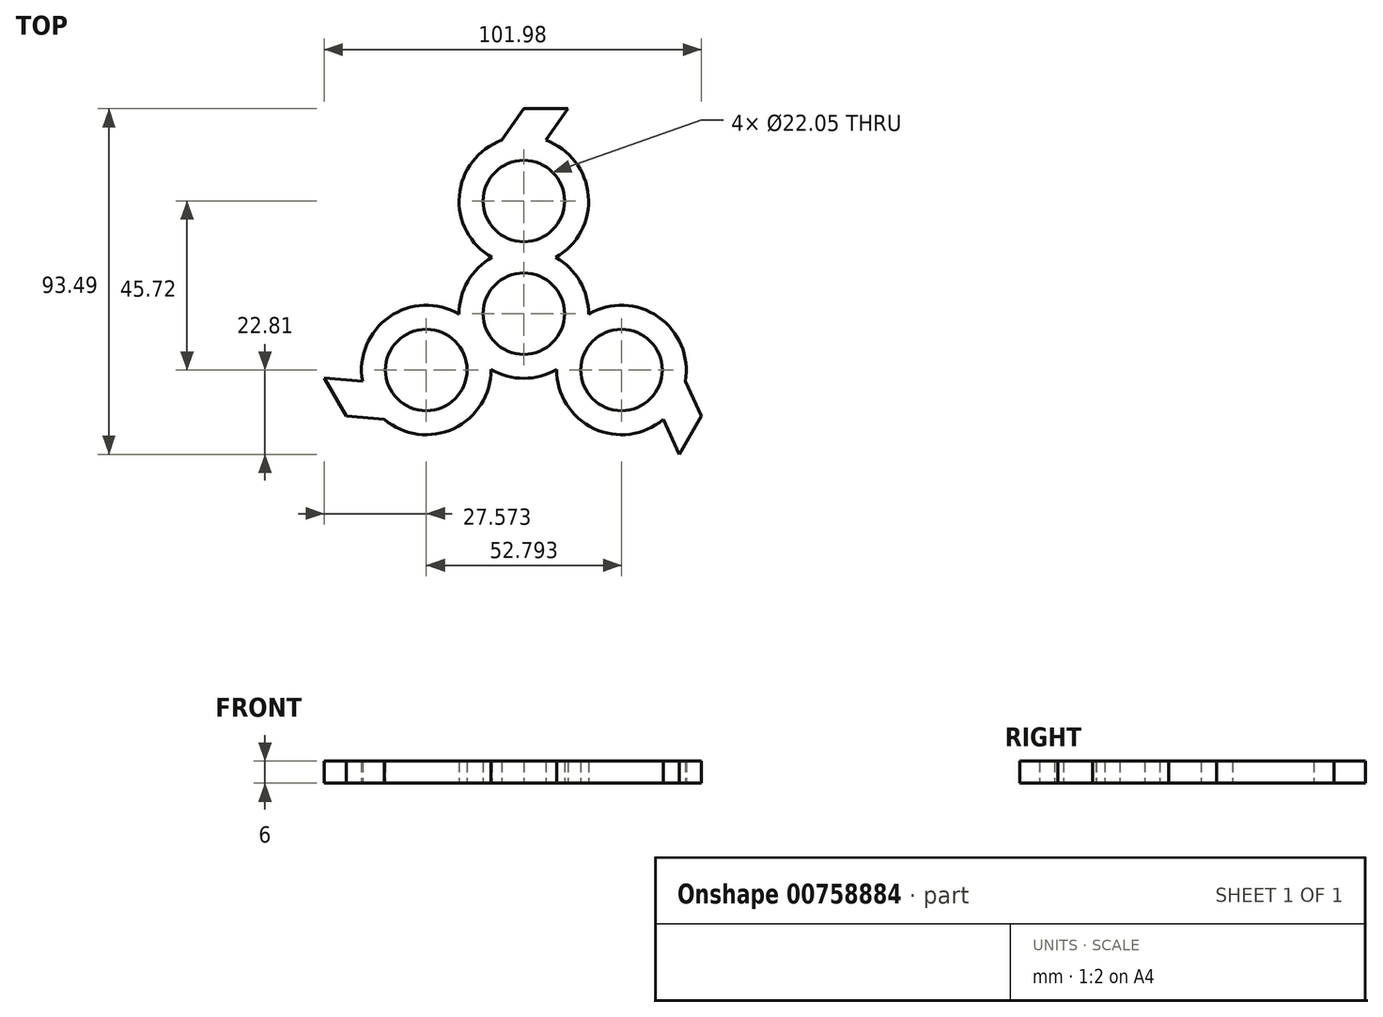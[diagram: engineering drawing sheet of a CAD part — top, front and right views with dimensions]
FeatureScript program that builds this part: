
annotation { "Feature Type Name" : "Feature", "Feature Type Description" : "" }
export const myFeature = defineFeature(function(context is Context, id is Id, definition is map)
    precondition{}
    {
        {
            var Q0;
            Q0=qCreatedBy(makeId("Top.planeOp"),FACE);
            var sketch = newSketch(context, id + "F0", { "sketchPlane" : qUnion([Q0])});
            skCircle(sketch, "E0", {"center": v(0, 30.48) * mm, "radius": 11.03 * mm});
            skCircle(sketch, "E1", {"center": v(0, 0) * mm, "radius": 11.03 * mm});
            skArc(sketch, "E2", {"start": v(8.6, 15.24) * mm, "mid": v(17.44, 31.93) * mm, "end": v(5.96, 46.93) * mm});
            skArc(sketch, "E3", {"start": v(-8.9, -15.07) * mm, "mid": v(0, -17.5) * mm, "end": v(8.9, -15.07) * mm});
            skArc(sketch, "E4.1.0", {"start": v(-17.5, -0.17) * mm, "mid": v(-36.37, -0.86) * mm, "end": v(-43.63, -18.3) * mm});
            skCircle(sketch, "E4.1.1", {"center": v(-26.4, -15.24) * mm, "radius": 11.03 * mm});
            skArc(sketch, "E4.2.0", {"start": v(8.9, -15.07) * mm, "mid": v(18.93, -31.07) * mm, "end": v(37.66, -28.63) * mm});
            skCircle(sketch, "E4.2.1", {"center": v(26.4, -15.24) * mm, "radius": 11.03 * mm});
            skArc(sketch, "E5.trimOffspring", {"start": v(17.5, -0.17) * mm, "mid": v(15.16, 8.75) * mm, "end": v(8.6, 15.24) * mm});
            skArc(sketch, "E6.trimOffspring", {"start": v(-8.6, 15.24) * mm, "mid": v(-15.16, 8.75) * mm, "end": v(-17.5, -0.17) * mm});
            skLineSegment(sketch, "E7", {"start": v(0, 30.48) * mm, "end": v(-17.5, 30.48) * mm, "construction": true});
            skLineSegment(sketch, "E8", {"start": v(-5.96, 46.93) * mm, "end": v(0, 55.44) * mm});
            skArc(sketch, "E9.trimOffspring", {"start": v(-5.96, 46.93) * mm, "mid": v(-17.44, 31.93) * mm, "end": v(-8.6, 15.24) * mm});
            skPoint(sketch, "E10.end.orphan", {"position": v(17.5, 30.48) * mm});
            skLineSegment(sketch, "E11", {"start": v(5.96, 46.93) * mm, "end": v(11.92, 55.44) * mm});
            skLineSegment(sketch, "E12", {"start": v(11.92, 55.44) * mm, "end": v(0, 55.44) * mm});
            skLineSegment(sketch, "E13.1.0", {"start": v(-37.66, -28.63) * mm, "end": v(-48, -27.72) * mm});
            skLineSegment(sketch, "E13.1.1", {"start": v(-53.97, -17.4) * mm, "end": v(-48, -27.72) * mm});
            skLineSegment(sketch, "E13.1.2", {"start": v(-43.63, -18.3) * mm, "end": v(-53.97, -17.4) * mm});
            skLineSegment(sketch, "E13.2.0", {"start": v(43.63, -18.3) * mm, "end": v(48, -27.72) * mm});
            skLineSegment(sketch, "E13.2.1", {"start": v(42.05, -38.05) * mm, "end": v(48, -27.72) * mm});
            skLineSegment(sketch, "E13.2.2", {"start": v(37.66, -28.63) * mm, "end": v(42.05, -38.05) * mm});
            skArc(sketch, "E14.trimOffspring", {"start": v(-37.66, -28.63) * mm, "mid": v(-18.93, -31.07) * mm, "end": v(-8.9, -15.07) * mm});
            skArc(sketch, "E15.trimOffspring", {"start": v(43.63, -18.3) * mm, "mid": v(36.37, -0.86) * mm, "end": v(17.5, -0.17) * mm});
            skSolve(sketch);
        }
        {
            var Q0;
            Q0=makeQuery(id+"F0.imprint","IMPRINT",FACE,{"disambiguationData":[TD([[makeQuery(id+"F0.imprint","IMPRINT",EDGE,{"derivedFrom":sQuery(id+"F0.wireOp",EDGE,"E0")}),-1.0]])]});
            extrude(context, id + "F1", {"entities" : qUnion([Q0]), "depth" : 6 * mm, "offsetDistance" : 25.4 * mm});
        }
    });
